FCSTD DOCUMENT  (FreeCAD 1.0R38643 (Git))
Label: Acryl_B04
License: All rights reserved
LicenseURL: https://en.wikipedia.org/wiki/All_rights_reserved
objects: Sketcher::SketchObject×3, PartDesign::Body×1
note: 7 computed .brp shape members not serialized (recipe doc carries the construction recipe); baked Part::Feature solids carry a one-line shape summary decoded from their .brp

FEATURE [Sketcher::SketchObject] Sketch
  ArcFitTolerance = 1e-06
  AttachmentSupport = -> [XY_Plane]
  FullyConstrained = false
  MakeInternals = false
  MapMode = 5
  sketch-geometry (44):
    g0: LineSegment StartX=-95.28 StartY=37.71 StartZ=0 EndX=-95.28 EndY=18.96 EndZ=0
    g1: LineSegment StartX=79.72 StartY=-57.29 StartZ=0 EndX=79.72 EndY=-38.54 EndZ=0
    g2: LineSegment StartX=79.72 StartY=37.71 StartZ=0 EndX=44.72 EndY=37.71 EndZ=0
    g3: LineSegment StartX=-55.28 StartY=37.7105 StartZ=0 EndX=-55.28 EndY=32.7105 EndZ=0
    g4: LineSegment StartX=-55.28 StartY=32.7105 StartZ=0 EndX=-45.28 EndY=32.7105 EndZ=0
    g5: LineSegment StartX=-45.28 StartY=32.7105 StartZ=0 EndX=-45.28 EndY=37.7105 EndZ=0
    g6: LineSegment StartX=-55.28 StartY=37.7105 StartZ=0 EndX=-95.28 EndY=37.71 EndZ=0
    g7: LineSegment StartX=-10.28 StartY=37.7105 StartZ=0 EndX=-10.28 EndY=32.7105 EndZ=0
    g8: LineSegment StartX=-10.28 StartY=32.7105 StartZ=0 EndX=-0.28 EndY=32.7105 EndZ=0
    g9: LineSegment StartX=-0.28 StartY=32.7105 StartZ=0 EndX=-0.28 EndY=37.7105 EndZ=0
    g10: LineSegment StartX=-10.28 StartY=37.7105 StartZ=0 EndX=-45.28 EndY=37.7105 EndZ=0
    g11: LineSegment StartX=34.72 StartY=37.7105 StartZ=0 EndX=34.72 EndY=32.7105 EndZ=0
    g12: LineSegment StartX=34.72 StartY=32.7105 StartZ=0 EndX=44.72 EndY=32.7105 EndZ=0
    g13: LineSegment StartX=44.72 StartY=32.7105 StartZ=0 EndX=44.72 EndY=37.7105 EndZ=0
    g14: LineSegment StartX=34.72 StartY=37.7105 StartZ=0 EndX=-0.28 EndY=37.7105 EndZ=0
    g15: LineSegment StartX=-95.28 StartY=-57.29 StartZ=0 EndX=-55.28 EndY=-57.29 EndZ=0
    g16: LineSegment StartX=-45.28 StartY=-57.2895 StartZ=0 EndX=-45.28 EndY=-52.2895 EndZ=0
    g17: LineSegment StartX=-45.28 StartY=-52.2895 StartZ=0 EndX=-55.28 EndY=-52.2895 EndZ=0
    g18: LineSegment StartX=-55.28 StartY=-52.2895 StartZ=0 EndX=-55.28 EndY=-57.2895 EndZ=0
    g19: LineSegment StartX=-45.28 StartY=-57.2895 StartZ=0 EndX=-10.28 EndY=-57.2895 EndZ=0
    g20: LineSegment StartX=-0.28 StartY=-57.2895 StartZ=0 EndX=-0.28 EndY=-52.2895 EndZ=0
    g21: LineSegment StartX=-0.28 StartY=-52.2895 StartZ=0 EndX=-10.28 EndY=-52.2895 EndZ=0
    g22: LineSegment StartX=-10.28 StartY=-52.2895 StartZ=0 EndX=-10.28 EndY=-57.2895 EndZ=0
    g23: LineSegment StartX=-0.28 StartY=-57.2895 StartZ=0 EndX=34.72 EndY=-57.2895 EndZ=0
    g24: LineSegment StartX=44.72 StartY=-57.2895 StartZ=0 EndX=44.72 EndY=-52.2895 EndZ=0
    g25: LineSegment StartX=44.72 StartY=-52.2895 StartZ=0 EndX=34.72 EndY=-52.2895 EndZ=0
    g26: LineSegment StartX=34.72 StartY=-52.2895 StartZ=0 EndX=34.72 EndY=-57.2895 EndZ=0
    g27: LineSegment StartX=44.72 StartY=-57.2895 StartZ=0 EndX=79.72 EndY=-57.29 EndZ=0
    g28: LineSegment StartX=-95.28 StartY=8.96 StartZ=0 EndX=-90.28 EndY=8.96 EndZ=0
    g29: LineSegment StartX=-90.28 StartY=8.96 StartZ=0 EndX=-90.28 EndY=18.96 EndZ=0
    g30: LineSegment StartX=-90.28 StartY=18.96 StartZ=0 EndX=-95.28 EndY=18.96 EndZ=0
    g31: LineSegment StartX=-95.28 StartY=-38.54 StartZ=0 EndX=-90.28 EndY=-38.54 EndZ=0
    g32: LineSegment StartX=-90.28 StartY=-38.54 StartZ=0 EndX=-90.28 EndY=-28.54 EndZ=0
    g33: LineSegment StartX=-90.28 StartY=-28.54 StartZ=0 EndX=-95.28 EndY=-28.54 EndZ=0
    g34: LineSegment StartX=79.72 StartY=18.96 StartZ=0 EndX=74.72 EndY=18.96 EndZ=0
    g35: LineSegment StartX=74.72 StartY=18.96 StartZ=0 EndX=74.72 EndY=8.96 EndZ=0
    g36: LineSegment StartX=74.72 StartY=8.96 StartZ=0 EndX=79.72 EndY=8.96 EndZ=0
    g37: LineSegment StartX=79.72 StartY=-28.54 StartZ=0 EndX=74.72 EndY=-28.54 EndZ=0
    g38: LineSegment StartX=74.72 StartY=-28.54 StartZ=0 EndX=74.72 EndY=-38.54 EndZ=0
    g39: LineSegment StartX=74.72 StartY=-38.54 StartZ=0 EndX=79.72 EndY=-38.54 EndZ=0
    g40: LineSegment StartX=-95.28 StartY=8.96 StartZ=0 EndX=-95.28 EndY=-28.54 EndZ=0
    g41: LineSegment StartX=-95.28 StartY=-38.54 StartZ=0 EndX=-95.28 EndY=-57.29 EndZ=0
    g42: LineSegment StartX=79.72 StartY=18.96 StartZ=0 EndX=79.72 EndY=37.71 EndZ=0
    g43: LineSegment StartX=79.72 StartY=-28.54 StartZ=0 EndX=79.72 EndY=8.96 EndZ=0
  constraints (114):
    c: Coincident(g42,g2)
    c: Coincident(g6,g0)
    c: Vertical(g0)
    c: Vertical(g1)
    c: Horizontal(g2)
    c: Distance(g0,g42) = 175
    c: Distance(g41,g6) = 95
    c: Coincident(g3,g4)
    c: Coincident(g4,g5)
    c: Vertical(g3)
    c: Vertical(g5)
    c: Horizontal(g4)
    c: Distance(g3,g5) = 10
    c: Distance(g4,g3) = 5
    c: PointOnObject(g3,g6)
    c: PointOnObject(g10,g5)
    c: PointOnObject(g6,g3)
    c: Coincident(g7,g8)
    c: Coincident(g8,g9)
    c: Vertical(g7)
    c: Vertical(g9)
    c: Horizontal(g8)
    c: Distance(g7,g9) = 10
    c: Distance(g8,g7) = 5
    c: PointOnObject(g7,g10)
    c: PointOnObject(g14,g9)
    c: PointOnObject(g10,g7)
    c: Coincident(g11,g12)
    c: Coincident(g12,g13)
    c: Vertical(g11)
    c: Vertical(g13)
    c: Horizontal(g12)
    c: Distance(g11,g13) = 10
    c: Distance(g12,g11) = 5
    c: PointOnObject(g11,g14)
    c: PointOnObject(g2,g13)
    c: PointOnObject(g14,g11)
    c: DistanceX(g4,g7) = 35
    c: DistanceX(g8,g11) = 35
    c: DistanceX(g0,g3) = 40
    c: DistanceY(g1,g42) = 95
    c: Coincident(g15,g41)
    c: Coincident(g27,g1)
    c: Horizontal(g15)
    c: Coincident(g16,g17)
    c: Coincident(g17,g18)
    c: Horizontal(g17)
    c: Vertical(g16)
    c: Vertical(g18)
    c: Distance(g16,g18) = 10
    c: Distance(g18,g17) = 5
    c: Vertical(g17,g3)
    c: Vertical(g15,g17)
    c: Coincident(g20,g21)
    c: Coincident(g21,g22)
    c: Horizontal(g21)
    c: Vertical(g20)
    c: Vertical(g22)
    c: Distance(g20,g22) = 10
    c: Distance(g22,g21) = 5
    c: Vertical(g21,g7)
    c: Coincident(g24,g25)
    c: Coincident(g25,g26)
    c: Horizontal(g25)
    c: Vertical(g24)
    c: Vertical(g26)
    c: Distance(g24,g26) = 10
    c: Distance(g26,g25) = 5
    c: Vertical(g25,g11)
    c: Coincident(g19,g16)
    c: Coincident(g19,g22)
    c: Coincident(g23,g20)
    c: Coincident(g23,g26)
    c: Coincident(g24,g27)
    c: DistanceY(g-1,g0) = 37.71
    c: DistanceX(g41,g-1) = 95.28
    c: DistanceY(g-1,g42) = 37.71
    c: Coincident(g28,g29)
    c: Coincident(g29,g30)
    c: Vertical(g29)
    c: Horizontal(g28)
    c: Horizontal(g30)
    c: Distance(g30,g29) = 5
    c: Distance(g28,g30) = 10
    c: DistanceY(g30,g0) = 18.75
    c: Coincident(g31,g32)
    c: Coincident(g32,g33)
    c: Vertical(g32)
    c: Horizontal(g31)
    c: Horizontal(g33)
    c: Distance(g33,g32) = 5
    c: Distance(g31,g33) = 10
    c: DistanceY(g41,g31) = 18.75
    c: Coincident(g34,g35)
    c: Coincident(g35,g36)
    c: Horizontal(g34)
    c: Horizontal(g36)
    c: Vertical(g35)
    c: Distance(g35,g34) = 5
    c: Distance(g34,g36) = 10
    c: PointOnObject(g34,g42)
    c: DistanceY(g34,g42) = 18.75
    c: Coincident(g37,g38)
    c: Coincident(g38,g39)
    c: Vertical(g38)
    c: Horizontal(g37)
    c: Horizontal(g39)
    c: Distance(g39,g38) = 5
    c: Distance(g37,g39) = 10
    c: DistanceY(g1,g39) = 18.75
    c: Coincident(g40,g33)
    c: PointOnObject(g41,g31)
    c: PointOnObject(g43,g36)
    c: PointOnObject(g42,g34)
FEATURE [Sketcher::SketchObject] Sketch001
  ArcFitTolerance = 1e-06
  AttachmentSupport = -> [XY_Plane]
  ExternalGeometry = -> [Sketch]
  FullyConstrained = false
  MakeInternals = false
  MapMode = 5
  sketch-geometry (51):
    g0: LineSegment StartX=-95.2826 StartY=-69.6326 StartZ=0 EndX=-95.2826 EndY=-94.6326 EndZ=0
    g1: LineSegment StartX=-95.2826 StartY=-129.633 StartZ=0 EndX=-55.1826 EndY=-129.633 EndZ=0
    g2: LineSegment StartX=79.7174 StartY=-129.633 StartZ=0 EndX=79.7174 EndY=-104.633 EndZ=0
    g3: LineSegment StartX=79.7174 StartY=-69.6326 StartZ=0 EndX=44.6174 EndY=-69.6326 EndZ=0
    g4: LineSegment StartX=-45.3826 StartY=-69.6326 StartZ=0 EndX=-45.3826 EndY=-64.6326 EndZ=0
    g5: LineSegment StartX=-45.3826 StartY=-64.6326 StartZ=0 EndX=-55.1826 EndY=-64.6326 EndZ=0
    g6: LineSegment StartX=-55.1826 StartY=-64.6326 StartZ=0 EndX=-55.1826 EndY=-69.6326 EndZ=0
    g7: LineSegment StartX=-0.382584 StartY=-69.6326 StartZ=0 EndX=-0.382584 EndY=-64.6326 EndZ=0
    g8: LineSegment StartX=-0.382584 StartY=-64.6326 StartZ=0 EndX=-10.1826 EndY=-64.6326 EndZ=0
    g9: LineSegment StartX=-10.1826 StartY=-64.6326 StartZ=0 EndX=-10.1826 EndY=-69.6326 EndZ=0
    g10: LineSegment StartX=44.6174 StartY=-69.6326 StartZ=0 EndX=44.6174 EndY=-64.6326 EndZ=0
    g11: LineSegment StartX=44.6174 StartY=-64.6326 StartZ=0 EndX=34.8174 EndY=-64.6326 EndZ=0
    g12: LineSegment StartX=34.8174 StartY=-64.6326 StartZ=0 EndX=34.8174 EndY=-69.6326 EndZ=0
    g13: LineSegment StartX=-55.1826 StartY=-129.633 StartZ=0 EndX=-55.1826 EndY=-134.633 EndZ=0
    g14: LineSegment StartX=-55.1826 StartY=-134.633 StartZ=0 EndX=-45.3826 EndY=-134.633 EndZ=0
    g15: LineSegment StartX=-45.3826 StartY=-134.633 StartZ=0 EndX=-45.3826 EndY=-129.633 EndZ=0
    g16: LineSegment StartX=-10.1826 StartY=-129.633 StartZ=0 EndX=-10.1826 EndY=-134.633 EndZ=0
    g17: LineSegment StartX=-10.1826 StartY=-134.633 StartZ=0 EndX=-0.382584 EndY=-134.633 EndZ=0
    g18: LineSegment StartX=-0.382584 StartY=-134.633 StartZ=0 EndX=-0.382584 EndY=-129.633 EndZ=0
    g19: LineSegment StartX=34.8174 StartY=-129.633 StartZ=0 EndX=34.8174 EndY=-134.633 EndZ=0
    g20: LineSegment StartX=34.8174 StartY=-134.633 StartZ=0 EndX=44.6174 EndY=-134.633 EndZ=0
    g21: LineSegment StartX=44.6174 StartY=-134.633 StartZ=0 EndX=44.6174 EndY=-129.633 EndZ=0
    g22: LineSegment StartX=-95.2826 StartY=-104.633 StartZ=0 EndX=-90.2826 EndY=-104.633 EndZ=0
    g23: LineSegment StartX=-90.2826 StartY=-104.633 StartZ=0 EndX=-90.2826 EndY=-94.6326 EndZ=0
    g24: LineSegment StartX=-90.2826 StartY=-94.6326 StartZ=0 EndX=-95.2826 EndY=-94.6326 EndZ=0
    g25: LineSegment StartX=79.7174 StartY=-94.6326 StartZ=0 EndX=74.7174 EndY=-94.6326 EndZ=0
    g26: LineSegment StartX=74.7174 StartY=-94.6326 StartZ=0 EndX=74.7174 EndY=-104.633 EndZ=0
    g27: LineSegment StartX=74.7174 StartY=-104.633 StartZ=0 EndX=79.7174 EndY=-104.633 EndZ=0
    g28: LineSegment [constr] StartX=-95.2826 StartY=-99.6326 StartZ=0 EndX=79.7174 EndY=-99.6326 EndZ=0
    g29: LineSegment StartX=-84.847 StartY=-106.133 StartZ=0 EndX=-65.847 EndY=-106.133 EndZ=0
    g30: LineSegment StartX=-65.847 StartY=-106.133 StartZ=0 EndX=-65.847 EndY=-93.1326 EndZ=0
    g31: LineSegment StartX=-65.847 StartY=-93.1326 StartZ=0 EndX=-84.847 EndY=-93.1326 EndZ=0
    g32: LineSegment StartX=-84.847 StartY=-93.1326 StartZ=0 EndX=-84.847 EndY=-106.133 EndZ=0
    g33: GeomPoint [constr] X=-75.347 Y=-99.6326 Z=0
    g34: LineSegment StartX=-42.984 StartY=-107.133 StartZ=0 EndX=62.016 EndY=-107.133 EndZ=0
    g35: LineSegment StartX=62.016 StartY=-107.133 StartZ=0 EndX=62.016 EndY=-92.1326 EndZ=0
    g36: LineSegment StartX=62.016 StartY=-92.1326 StartZ=0 EndX=-42.984 EndY=-92.1326 EndZ=0
    g37: LineSegment StartX=-42.984 StartY=-92.1326 StartZ=0 EndX=-42.984 EndY=-107.133 EndZ=0
    g38: GeomPoint [constr] X=9.51598 Y=-99.6326 Z=0
    g39: Circle CenterX=-78.024 CenterY=-83.1326 CenterZ=0 NormalX=0 NormalY=0 NormalZ=1 AngleXU=0 Radius=3.75
    g40: Circle CenterX=-55.3525 CenterY=-83.1326 CenterZ=0 NormalX=0 NormalY=0 NormalZ=1 AngleXU=0 Radius=3.75
    g41: Circle CenterX=-78.024 CenterY=-116.133 CenterZ=0 NormalX=0 NormalY=0 NormalZ=1 AngleXU=0 Radius=3
    g42: Circle CenterX=-55.3525 CenterY=-116.133 CenterZ=0 NormalX=0 NormalY=0 NormalZ=1 AngleXU=0 Radius=2.75
    g43: LineSegment StartX=-55.1826 StartY=-69.6326 StartZ=0 EndX=-95.2826 EndY=-69.6326 EndZ=0
    g44: LineSegment StartX=-10.1826 StartY=-69.6326 StartZ=0 EndX=-45.3826 EndY=-69.6326 EndZ=0
    g45: LineSegment StartX=34.8174 StartY=-69.6326 StartZ=0 EndX=-0.382584 EndY=-69.6326 EndZ=0
    g46: LineSegment StartX=79.7174 StartY=-94.6326 StartZ=0 EndX=79.7174 EndY=-69.6326 EndZ=0
    g47: LineSegment StartX=44.6174 StartY=-129.633 StartZ=0 EndX=79.7174 EndY=-129.633 EndZ=0
    g48: LineSegment StartX=-0.382584 StartY=-129.633 StartZ=0 EndX=34.8174 EndY=-129.633 EndZ=0
    g49: LineSegment StartX=-45.3826 StartY=-129.633 StartZ=0 EndX=-10.1826 EndY=-129.633 EndZ=0
    g50: LineSegment StartX=-95.2826 StartY=-104.633 StartZ=0 EndX=-95.2826 EndY=-129.633 EndZ=0
  constraints (124):
    c: Coincident(g50,g1)
    c: Coincident(g47,g2)
    c: Coincident(g46,g3)
    c: Coincident(g43,g0)
    c: Vertical(g0)
    c: Vertical(g2)
    c: Horizontal(g1)
    c: Horizontal(g3)
    c: Distance(g0,g46) = 175
    c: Distance(g1,g43) = 60
    c: Coincident(g4,g5)
    c: Coincident(g5,g6)
    c: Horizontal(g5)
    c: Vertical(g4)
    c: Vertical(g6)
    c: Distance(g4,g6) = 9.8
    c: Distance(g6,g5) = 5
    c: PointOnObject(g6,g43)
    c: DistanceX(g0,g6) = 40.1
    c: Coincident(g7,g8)
    c: Coincident(g8,g9)
    c: Horizontal(g8)
    c: Vertical(g7)
    c: Vertical(g9)
    c: Distance(g7,g9) = 9.8
    c: Distance(g9,g8) = 5
    c: PointOnObject(g9,g44)
    c: DistanceX(g4,g8) = 35.2
    c: Coincident(g10,g11)
    c: Coincident(g11,g12)
    c: Horizontal(g11)
    c: Vertical(g10)
    c: Vertical(g12)
    c: Distance(g10,g12) = 9.8
    c: Distance(g12,g11) = 5
    c: PointOnObject(g12,g45)
    c: DistanceX(g7,g11) = 35.2
    c: Coincident(g13,g14)
    c: Coincident(g14,g15)
    c: Vertical(g13)
    c: Vertical(g15)
    c: Horizontal(g14)
    c: Distance(g13,g15) = 9.8
    c: Distance(g14,g13) = 5
    c: Vertical(g13,g6)
    c: Coincident(g16,g17)
    c: Coincident(g17,g18)
    c: Vertical(g16)
    c: Vertical(g18)
    c: Horizontal(g17)
    c: Distance(g16,g18) = 9.8
    c: Distance(g17,g16) = 5
    c: Vertical(g16,g9)
    c: Coincident(g19,g20)
    c: Coincident(g20,g21)
    c: Vertical(g19)
    c: Vertical(g21)
    c: Horizontal(g20)
    c: Distance(g19,g21) = 9.8
    c: Distance(g20,g19) = 5
    c: Vertical(g19,g12)
    c: Coincident(g22,g23)
    c: Coincident(g23,g24)
    c: Vertical(g23)
    c: Horizontal(g22)
    c: Horizontal(g24)
    c: Distance(g24,g23) = 5
    c: Distance(g22,g24) = 10
    c: DistanceY(g24,g0) = 25
    c: Coincident(g25,g26)
    c: Coincident(g26,g27)
    c: Horizontal(g25)
    c: Horizontal(g27)
    c: Vertical(g26)
    c: Distance(g26,g25) = 5
    c: Distance(g25,g27) = 10
    c: PointOnObject(g25,g46)
    c: DistanceY(g25,g46) = 25
    c: Symmetric(g0,g50,g28)
    c: Symmetric(g2,g46,g28)
    c: Coincident(g29,g30)
    c: Coincident(g30,g31)
    c: Coincident(g31,g32)
    c: Coincident(g32,g29)
    c: Horizontal(g29)
    c: Horizontal(g31)
    c: Vertical(g30)
    c: Vertical(g32)
    c: Symmetric(g31,g29,g33)
    c: Distance(g30,g32) = 19
    c: Distance(g29,g31) = 13
    c: PointOnObject(g33,g28)
    c: Coincident(g34,g35)
    c: Coincident(g35,g36)
    c: Coincident(g36,g37)
    c: Coincident(g37,g34)
    c: Horizontal(g34)
    c: Horizontal(g36)
    c: Vertical(g35)
    c: Vertical(g37)
    c: Symmetric(g36,g34,g38)
    c: Distance(g35,g37) = 105
    c: Distance(g34,g36) = 15
    c: PointOnObject(g38,g28)
    c: Diameter(g39) = 7.5
    c: DistanceY(g31,g39) = 10
    c: Diameter(g40) = 7.5
    c: Horizontal(g39,g40)
    c: Diameter(g41) = 6
    c: Vertical(g39,g41)
    c: DistanceY(g41,g29) = 10
    c: Diameter(g42) = 5.5
    c: Horizontal(g42,g41)
    c: Vertical(g42,g40)
    c: PointOnObject(g46,g25)
    c: PointOnObject(g2,g27)
    c: Coincident(g48,g19)
    c: PointOnObject(g47,g21)
    c: Coincident(g49,g16)
    c: PointOnObject(g48,g18)
    c: Coincident(g1,g13)
    c: PointOnObject(g49,g15)
    c: Coincident(g0,g24)
    c: PointOnObject(g50,g22)
FEATURE [Sketcher::SketchObject] Sketch002
  ArcFitTolerance = 1e-06
  AttachmentSupport = -> [XY_Plane]
  ExternalGeometry = -> [Sketch,Sketch001]
  FullyConstrained = false
  MakeInternals = false
  MapMode = 5
  sketch-geometry (30):
    g0: LineSegment StartX=98.1372 StartY=32.71 StartZ=0 EndX=98.1372 EndY=-52.29 EndZ=0
    g1: LineSegment StartX=98.1372 StartY=-52.29 StartZ=0 EndX=158.137 EndY=-52.29 EndZ=0
    g2: LineSegment StartX=158.137 StartY=-52.29 StartZ=0 EndX=158.137 EndY=32.71 EndZ=0
    g3: LineSegment StartX=158.137 StartY=32.71 StartZ=0 EndX=98.1372 EndY=32.71 EndZ=0
    g4: LineSegment StartX=98.1372 StartY=18.97 StartZ=0 EndX=93.1372 EndY=18.97 EndZ=0
    g5: LineSegment StartX=93.1372 StartY=18.97 StartZ=0 EndX=93.1372 EndY=9.17 EndZ=0
    g6: LineSegment StartX=93.1372 StartY=9.17 StartZ=0 EndX=98.1372 EndY=9.17 EndZ=0
    g7: LineSegment StartX=98.1372 StartY=9.17 StartZ=0 EndX=98.1372 EndY=18.97 EndZ=0
    g8: LineSegment StartX=98.1372 StartY=-38.55 StartZ=0 EndX=98.1372 EndY=-28.75 EndZ=0
    g9: LineSegment StartX=98.1372 StartY=-28.75 StartZ=0 EndX=93.1372 EndY=-28.75 EndZ=0
    g10: LineSegment StartX=93.1372 StartY=-28.75 StartZ=0 EndX=93.1372 EndY=-38.55 EndZ=0
    g11: LineSegment StartX=93.1372 StartY=-38.55 StartZ=0 EndX=98.1372 EndY=-38.55 EndZ=0
    g12: LineSegment StartX=158.137 StartY=18.97 StartZ=0 EndX=158.137 EndY=9.17 EndZ=0
    g13: LineSegment StartX=158.137 StartY=9.17 StartZ=0 EndX=163.137 EndY=9.17 EndZ=0
    g14: LineSegment StartX=163.137 StartY=9.17 StartZ=0 EndX=163.137 EndY=18.97 EndZ=0
    g15: LineSegment StartX=163.137 StartY=18.97 StartZ=0 EndX=158.137 EndY=18.97 EndZ=0
    g16: LineSegment StartX=158.137 StartY=-28.75 StartZ=0 EndX=158.137 EndY=-38.55 EndZ=0
    g17: LineSegment StartX=158.137 StartY=-38.55 StartZ=0 EndX=163.137 EndY=-38.55 EndZ=0
    g18: LineSegment StartX=163.137 StartY=-38.55 StartZ=0 EndX=163.137 EndY=-28.75 EndZ=0
    g19: LineSegment StartX=163.137 StartY=-28.75 StartZ=0 EndX=158.137 EndY=-28.75 EndZ=0
    g20: LineSegment StartX=123.237 StartY=27.71 StartZ=0 EndX=133.037 EndY=27.71 EndZ=0
    g21: LineSegment StartX=133.037 StartY=27.71 StartZ=0 EndX=133.037 EndY=37.71 EndZ=0
    g22: LineSegment StartX=133.037 StartY=37.71 StartZ=0 EndX=123.237 EndY=37.71 EndZ=0
    g23: LineSegment StartX=123.237 StartY=37.71 StartZ=0 EndX=123.237 EndY=27.71 EndZ=0
    g24: GeomPoint [constr] X=128.137 Y=32.71 Z=0
    g25: LineSegment StartX=123.237 StartY=-57.29 StartZ=0 EndX=133.037 EndY=-57.29 EndZ=0
    g26: LineSegment StartX=133.037 StartY=-57.29 StartZ=0 EndX=133.037 EndY=-47.29 EndZ=0
    g27: LineSegment StartX=133.037 StartY=-47.29 StartZ=0 EndX=123.237 EndY=-47.29 EndZ=0
    g28: LineSegment StartX=123.237 StartY=-47.29 StartZ=0 EndX=123.237 EndY=-57.29 EndZ=0
    g29: GeomPoint [constr] X=128.137 Y=-52.29 Z=0
  constraints (83):
    c: Coincident(g0,g1)
    c: Coincident(g1,g2)
    c: Coincident(g2,g3)
    c: Coincident(g3,g0)
    c: Vertical(g0)
    c: Vertical(g2)
    c: Horizontal(g1)
    c: Horizontal(g3)
    c: Distance(g0,g2) = 60
    c: Distance(g1,g3) = 85
    c: DistanceY(g0,g-3) = 5
    c: Coincident(g4,g5)
    c: Coincident(g5,g6)
    c: Coincident(g6,g7)
    c: Coincident(g7,g4)
    c: Horizontal(g4)
    c: Horizontal(g6)
    c: Vertical(g5)
    c: Vertical(g7)
    c: Distance(g5,g7) = 5
    c: Distance(g4,g6) = 9.8
    c: PointOnObject(g4,g0)
    c: DistanceY(g4,g0) = 13.74
    c: DistanceY(g-4,g-3) = 18.75
    c: Coincident(g8,g9)
    c: Coincident(g9,g10)
    c: Coincident(g10,g11)
    c: Coincident(g11,g8)
    c: Vertical(g8)
    c: Vertical(g10)
    c: Horizontal(g9)
    c: Horizontal(g11)
    c: Distance(g8,g10) = 5
    c: Distance(g9,g11) = 9.8
    c: PointOnObject(g8,g0)
    c: DistanceY(g0,g8) = 13.74
    c: Coincident(g12,g13)
    c: Coincident(g13,g14)
    c: Coincident(g14,g15)
    c: Coincident(g15,g12)
    c: Vertical(g12)
    c: Vertical(g14)
    c: Horizontal(g13)
    c: Horizontal(g15)
    c: Distance(g12,g14) = 5
    c: Distance(g13,g15) = 9.8
    c: PointOnObject(g12,g2)
    c: Horizontal(g4,g12)
    c: Coincident(g16,g17)
    c: Coincident(g17,g18)
    c: Coincident(g18,g19)
    c: Coincident(g19,g16)
    c: Vertical(g16)
    c: Vertical(g18)
    c: Horizontal(g17)
    c: Horizontal(g19)
    c: Distance(g16,g18) = 5
    c: Distance(g17,g19) = 9.8
    c: Horizontal(g8,g16)
    c: Coincident(g20,g21)
    c: Coincident(g21,g22)
    c: Coincident(g22,g23)
    c: Coincident(g23,g20)
    c: Horizontal(g20)
    c: Horizontal(g22)
    c: Vertical(g21)
    c: Vertical(g23)
    c: Symmetric(g22,g20,g24)
    c: Distance(g21,g23) = 9.8
    c: Distance(g20,g22) = 10
    c: Symmetric(g3,g3,g24)
    c: Coincident(g25,g26)
    c: Coincident(g26,g27)
    c: Coincident(g27,g28)
    c: Coincident(g28,g25)
    c: Horizontal(g25)
    c: Horizontal(g27)
    c: Vertical(g26)
    c: Vertical(g28)
    c: Symmetric(g27,g25,g29)
    c: Distance(g26,g28) = 9.8
    c: Distance(g25,g27) = 10
    c: Symmetric(g1,g1,g29)
FEATURE [PartDesign::Body] Body
  AllowCompound = false
  Group = -> [Sketch,Sketch001,Sketch002]
  Origin = -> Origin
